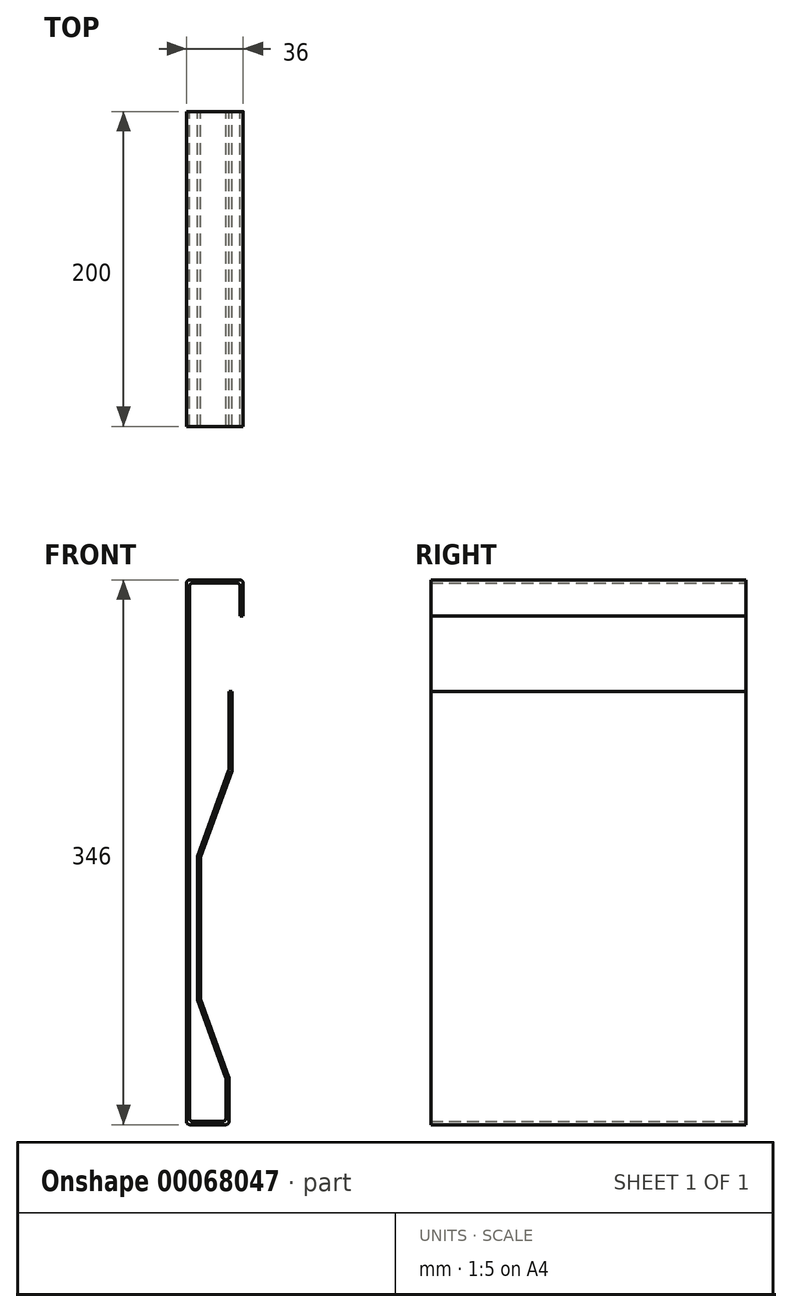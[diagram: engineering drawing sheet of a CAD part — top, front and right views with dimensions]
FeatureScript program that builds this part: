
annotation { "Feature Type Name" : "Feature", "Feature Type Description" : "" }
export const myFeature = defineFeature(function(context is Context, id is Id, definition is map)
    precondition{}
    {
        {
            var Q0;
            Q0=qCreatedBy(makeId("Front.planeOp"),FACE);
            var sketch = newSketch(context, id + "F0", { "sketchPlane" : qUnion([Q0])});
            skLineSegment(sketch, "E0", {"start": v(0, 0) * mm, "end": v(36, 0) * mm});
            skLineSegment(sketch, "E1", {"start": v(36, 0) * mm, "end": v(36, -23) * mm});
            skLineSegment(sketch, "E2", {"start": v(0, 0) * mm, "end": v(0, -346) * mm});
            skLineSegment(sketch, "E3", {"start": v(0, -346) * mm, "end": v(27, -346) * mm});
            skLineSegment(sketch, "E4", {"start": v(27, -316) * mm, "end": v(27, -346) * mm});
            skLineSegment(sketch, "E5.0", {"start": v(34, -2) * mm, "end": v(34, -23) * mm});
            skLineSegment(sketch, "E5.1", {"start": v(25, -316.35) * mm, "end": v(25, -344) * mm});
            skLineSegment(sketch, "E5.2", {"start": v(2, -344) * mm, "end": v(25, -344) * mm});
            skLineSegment(sketch, "E5.3", {"start": v(2, -2) * mm, "end": v(2, -344) * mm});
            skLineSegment(sketch, "E5.4", {"start": v(2, -2) * mm, "end": v(34, -2) * mm});
            skLineSegment(sketch, "E6", {"start": v(34, -23) * mm, "end": v(36, -23) * mm});
            skLineSegment(sketch, "E7", {"start": v(25, -316.35) * mm, "end": v(6.87, -266.55) * mm});
            skLineSegment(sketch, "E8", {"start": v(6.87, -266.55) * mm, "end": v(6.87, -175.85) * mm});
            skLineSegment(sketch, "E9", {"start": v(6.87, -175.85) * mm, "end": v(27, -120.56) * mm});
            skLineSegment(sketch, "E10", {"start": v(27, -120.56) * mm, "end": v(27, -70.9) * mm});
            skLineSegment(sketch, "E11.0", {"start": v(29, -120.9) * mm, "end": v(29, -70.9) * mm});
            skLineSegment(sketch, "E11.1", {"start": v(8.87, -176.2) * mm, "end": v(29, -120.9) * mm});
            skLineSegment(sketch, "E11.2", {"start": v(8.87, -266.2) * mm, "end": v(8.87, -176.2) * mm});
            skLineSegment(sketch, "E11.3", {"start": v(27, -316) * mm, "end": v(8.87, -266.2) * mm});
            skLineSegment(sketch, "E12", {"start": v(27, -70.9) * mm, "end": v(29, -70.9) * mm});
            skSolve(sketch);
        }
        {
            var Q0;
            Q0=qSketchRegion(id+"F0",true);
            extrude(context, id + "F1", {"entities" : qUnion([Q0]), "depth" : 200 * mm});
        }
        {
            var Q0;
            Q0=makeQuery(id+"F1.opExtrude","SWEPT_EDGE",EDGE,{"disambiguationData":[OSD([sQuery(id+"F0.wireOp",EDGE,"E0"),sQuery(id+"F0.wireOp",EDGE,"E2")])]});
            var Q1;
            Q1=makeQuery(id+"F1.opExtrude","SWEPT_EDGE",EDGE,{"disambiguationData":[OSD([sQuery(id+"F0.wireOp",EDGE,"E0"),sQuery(id+"F0.wireOp",EDGE,"E1")])]});
            var Q2;
            Q2=makeQuery(id+"F1.opExtrude","SWEPT_EDGE",EDGE,{"disambiguationData":[OSD([sQuery(id+"F0.wireOp",EDGE,"E5.0"),sQuery(id+"F0.wireOp",EDGE,"E5.4")])]});
            var Q3;
            Q3=makeQuery(id+"F1.opExtrude","SWEPT_EDGE",EDGE,{"disambiguationData":[OSD([sQuery(id+"F0.wireOp",EDGE,"E5.3"),sQuery(id+"F0.wireOp",EDGE,"E5.4")])]});
            var Q4;
            Q4=makeQuery(id+"F1.opExtrude","SWEPT_EDGE",EDGE,{"disambiguationData":[OSD([sQuery(id+"F0.wireOp",EDGE,"E2"),sQuery(id+"F0.wireOp",EDGE,"E3")])]});
            var Q5;
            Q5=makeQuery(id+"F1.opExtrude","SWEPT_EDGE",EDGE,{"disambiguationData":[OSD([sQuery(id+"F0.wireOp",EDGE,"E5.2"),sQuery(id+"F0.wireOp",EDGE,"E5.3")])]});
            var Q6;
            Q6=makeQuery(id+"F1.opExtrude","SWEPT_EDGE",EDGE,{"disambiguationData":[OSD([sQuery(id+"F0.wireOp",EDGE,"E3"),sQuery(id+"F0.wireOp",EDGE,"E4")])]});
            var Q7;
            Q7=makeQuery(id+"F1.opExtrude","SWEPT_EDGE",EDGE,{"disambiguationData":[OSD([sQuery(id+"F0.wireOp",EDGE,"E5.1"),sQuery(id+"F0.wireOp",EDGE,"E5.2")])]});
            var Q8;
            Q8=makeQuery(id+"F1.opExtrude","SWEPT_EDGE",EDGE,{"disambiguationData":[OSD([sQuery(id+"F0.wireOp",EDGE,"E5.1"),sQuery(id+"F0.wireOp",EDGE,"E7")])]});
            var Q9;
            Q9=makeQuery(id+"F1.opExtrude","SWEPT_EDGE",EDGE,{"disambiguationData":[OSD([sQuery(id+"F0.wireOp",EDGE,"E4"),sQuery(id+"F0.wireOp",EDGE,"E11.3")])]});
            var Q10;
            Q10=makeQuery(id+"F1.opExtrude","SWEPT_EDGE",EDGE,{"disambiguationData":[OSD([sQuery(id+"F0.wireOp",EDGE,"E11.2"),sQuery(id+"F0.wireOp",EDGE,"E11.3")])]});
            var Q11;
            Q11=makeQuery(id+"F1.opExtrude","SWEPT_EDGE",EDGE,{"disambiguationData":[OSD([sQuery(id+"F0.wireOp",EDGE,"E7"),sQuery(id+"F0.wireOp",EDGE,"E8")])]});
            var Q12;
            Q12=makeQuery(id+"F1.opExtrude","SWEPT_EDGE",EDGE,{"disambiguationData":[OSD([sQuery(id+"F0.wireOp",EDGE,"E8"),sQuery(id+"F0.wireOp",EDGE,"E9")])]});
            var Q13;
            Q13=makeQuery(id+"F1.opExtrude","SWEPT_EDGE",EDGE,{"disambiguationData":[OSD([sQuery(id+"F0.wireOp",EDGE,"E11.1"),sQuery(id+"F0.wireOp",EDGE,"E11.2")])]});
            var Q14;
            Q14=makeQuery(id+"F1.opExtrude","SWEPT_EDGE",EDGE,{"disambiguationData":[OSD([sQuery(id+"F0.wireOp",EDGE,"E11.0"),sQuery(id+"F0.wireOp",EDGE,"E11.1")])]});
            var Q15;
            Q15=makeQuery(id+"F1.opExtrude","SWEPT_EDGE",EDGE,{"disambiguationData":[OSD([sQuery(id+"F0.wireOp",EDGE,"E9"),sQuery(id+"F0.wireOp",EDGE,"E10")])]});
            fillet(context, id + "F2", {"entities" : qUnion([Q0, Q1, Q2, Q3, Q4, Q5, Q6, Q7, Q8, Q9, Q10, Q11, Q12, Q13, Q14, Q15]), "radius" : 2 * mm, "tangentPropagation" : true, "allowEdgeOverflow" : false});
        }
    });
